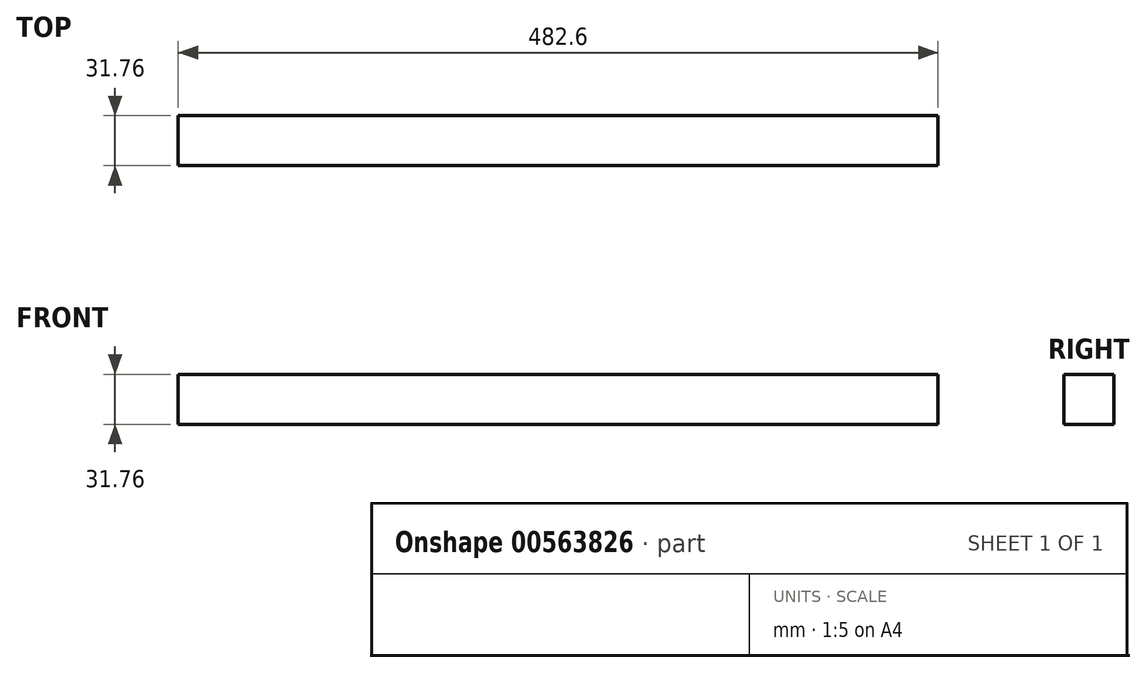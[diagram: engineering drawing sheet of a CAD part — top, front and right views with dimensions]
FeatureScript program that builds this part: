
annotation { "Feature Type Name" : "Feature", "Feature Type Description" : "" }
export const myFeature = defineFeature(function(context is Context, id is Id, definition is map)
    precondition{}
    {
        {
            var Q0;
            Q0=qCreatedBy(makeId("Front.planeOp"),FACE);
            var sketch = newSketch(context, id + "F0", { "sketchPlane" : qUnion([Q0])});
            skLineSegment(sketch, "E0.bottom", {"start": v(-241.3, 15.88) * mm, "end": v(241.3, 15.88) * mm});
            skLineSegment(sketch, "E0.top", {"start": v(-241.3, -15.87) * mm, "end": v(241.3, -15.87) * mm});
            skLineSegment(sketch, "E0.left", {"start": v(-241.3, 15.88) * mm, "end": v(-241.3, -15.87) * mm});
            skLineSegment(sketch, "E0.right", {"start": v(241.3, 15.88) * mm, "end": v(241.3, -15.87) * mm});
            skPoint(sketch, "E0.middle", {"position": v(0, 0) * mm});
            skSolve(sketch);
        }
        {
            var Q0;
            Q0=makeQuery(id+"F0.imprint","IMPRINT",FACE,{"disambiguationData":[TD([[makeQuery(id+"F0.imprint","IMPRINT",EDGE,{"derivedFrom":sQuery(id+"F0.wireOp",EDGE,"E0.bottom")}),-1.0]])]});
            extrude(context, id + "F1", {"entities" : qUnion([Q0]), "endBound" : BoundingType.SYMMETRIC, "depth" : 31.75 * mm, "offsetDistance" : 25.4 * mm});
        }
    });
